# Revit family: Flush_Valve_Toilet-Exposed-American_Standard-Selectronic-606X_Series
name_source: partatom
category: Plumbing Fixtures
revit_build: Autodesk Revit 2014 (Build: 20130308_1515(x64)
units: mm (PartAtom-declared; Revit-internal decimal feet)

## types (10) — shared parameters
ADA Compliant = Yes
Assembly Code = D2020100
CW Connection = Yes
CWFU = 10
Cold Water Connection Diameter = 1"
Cold Water Connection Height = 11 1/2"
Cold Water Connection Radius = 1/2"
Cold Water Connection Width = 4 3/4"
Default Elevation = 0"
HW Connection = No
Height = 16 1/2"
Installation Type = Exposed
Length = 2 1/4"
Manufacturer = American Standard
Material = Metal-American Standard-002-Polished Chrome
Price = Prices may vary. Please consult Manufacturer Representative for most up-to-date price list.
Product Documentation Link = https://www.americanstandard-us.com
Product Page URL = https://www.americanstandard-us.com
URL = http://www.americanstandard-us.com
Vent Connection = No
Warranty Information = 1 Year Limited Warranty
Waste Connection = No
Width = 2 7/8"
zero-valued in all types: HWFU, WFU

## per-type parameters (varying)
| type | Battery Life | Description | Flush Rate | Model |
| 6065.111 | 4 years @ 4,000 cycles per month (192,000 cycles) | American Standard Selectronic Sensor-Operated Toilet Flush Valve, 1.1 GPF Battery Powered. | 1.1 Gpf (4.2 Lpf) | 6065.111.002 |
| 6065.121 | 4 years @ 4,000 cycles per month (192,000 cycles) | American Standard Selectronic Sensor-Operated Toilet Flush Valve, 1.28 GPF Battery Powered. | 1.28 Gpf (4.8 Lpf) | 6065.121.002 |
| 6065.161 | 4 years @ 4,000 cycles per month (192,000 cycles) | American Standard Selectronic Sensor-Operated Toilet Flush Valve, 1.6 GPF  Battery Powered. | 1.6 Gpf (6.0 Lpf) | 6065.161.002 |
| 6065.761 | 4 years @ 4,000 cycles per month (192,000 cycles) | American Standard Selectronic Sensor-Operated Toilet Flush Valve, 1.1/1.6 GPF Battery Powered. | 1.1/1.6 Gpf | 6065.761.002 |
| 6065.721 | 4 years @ 4,000 cycles per month (192,000 cycles) | American Standard Selectronic Sensor-Operated Toilet Flush Valve, 1.28/1.1 GPF Battery Powered. | 1.28/1.1 Gpf | 6065.721.002 |
| 6066.111 | 10 years @ 4,000 cycles per month. | American Standard Selectronic Sensor-Operated Toilet Flush Valve, 1.1 GPF PWRX Battery Powered. | 1.1 Gpf (4.2 Lpf) | 6066.111.002 |
| 6066.121 | 10 years @ 4,000 cycles per month. | American Standard Selectronic Sensor-Operated Toilet Flush Valve, 1.28 GPF PWRX Battery Powered. | 1.28 Gpf (4.8 Lpf) | 6066.121.002 |
| 6066.161 | 10 years @ 4,000 cycles per month. | American Standard Selectronic Sensor-Operated Toilet Flush Valve, 1.6 GPF PWRX Battery Powered. | 1.6 Gpf (6.0 Lpf) | 6066.161.002 |
| 6066.721 | 10 years @ 4,000 cycles per month. | American Standard Selectronic Sensor-Operated Toilet Flush Valve, 1.28/1.1 GPF PWRX Battery Powered. | 1.28/1.1 Gpf | 6066.721.002 |
| 6066.761 | 10 years @ 4,000 cycles per month. | American Standard Selectronic Sensor-Operated Toilet Flush Valve, 1.1/1.6 GPF PWRX Battery Powered. | 1.1/1.6 Gpf | 6066.761.002 |

## geometry (parser evidence)
native form markers: Sweep x1
no freeform markers — native parametric forms only
